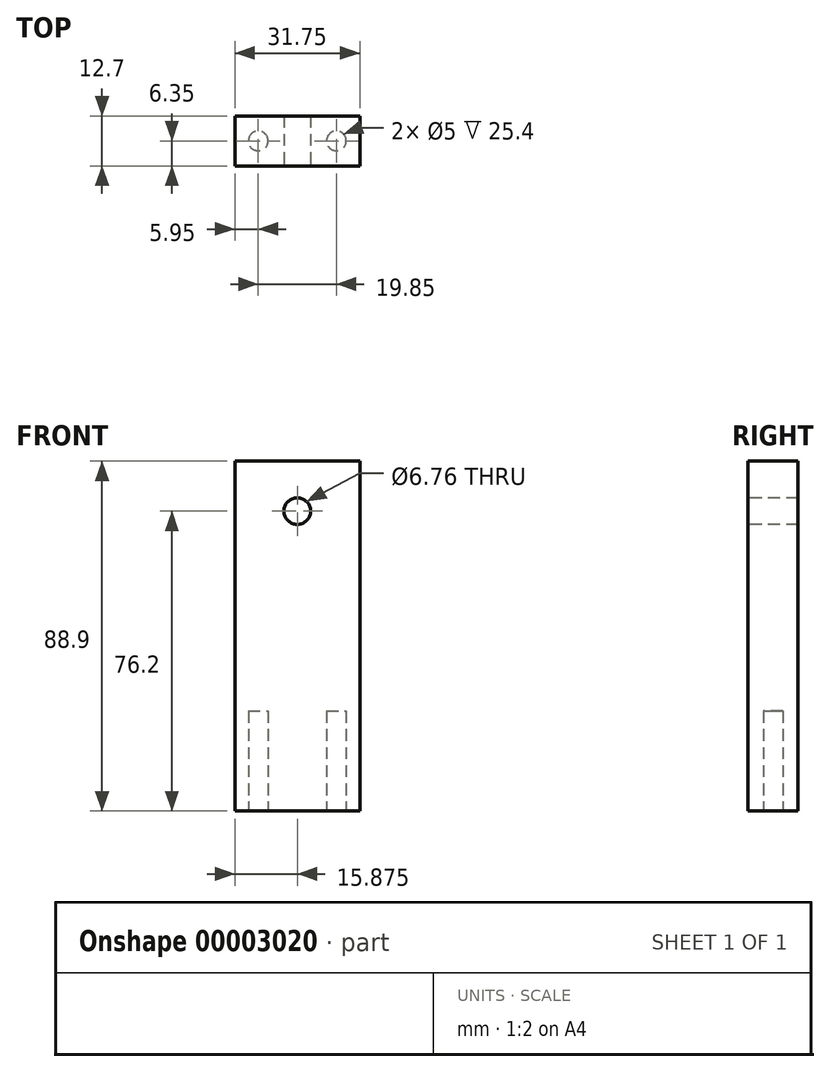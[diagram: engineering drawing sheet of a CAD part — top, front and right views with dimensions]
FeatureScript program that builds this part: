
annotation { "Feature Type Name" : "Feature", "Feature Type Description" : "" }
export const myFeature = defineFeature(function(context is Context, id is Id, definition is map)
    precondition{}
    {
        {
            var Q0;
            Q0=qCreatedBy(makeId("Top.planeOp"),FACE);
            var sketch = newSketch(context, id + "F0", { "sketchPlane" : qUnion([Q0])});
            skLineSegment(sketch, "E0.bottom", {"start": v(0, 0) * mm, "end": v(31.75, 0) * mm});
            skLineSegment(sketch, "E0.top", {"start": v(0, 12.7) * mm, "end": v(31.75, 12.7) * mm});
            skLineSegment(sketch, "E0.left", {"start": v(0, 0) * mm, "end": v(0, 12.7) * mm});
            skLineSegment(sketch, "E0.right", {"start": v(31.75, 0) * mm, "end": v(31.75, 12.7) * mm});
            skSolve(sketch);
        }
        {
            var Q0;
            Q0=makeQuery(id+"F0.imprint","IMPRINT",FACE,{"disambiguationData":[TD([[makeQuery(id+"F0.imprint","IMPRINT",EDGE,{"derivedFrom":sQuery(id+"F0.wireOp",EDGE,"E0.bottom")}),1.0]])]});
            extrude(context, id + "F1", {"entities" : qUnion([Q0]), "depth" : 88.9 * mm});
        }
        {
            var Q0;
            Q0=makeQuery(id+"F1.opExtrude","SWEPT_FACE",FACE,{"disambiguationData":[OSD([sQuery(id+"F0.wireOp",EDGE,"E0.bottom")])]});
            var sketch = newSketch(context, id + "F2", { "sketchPlane" : qUnion([Q0])});
            skCircle(sketch, "E1", {"center": v(15.88, 76.2) * mm, "radius": 3.38 * mm});
            skSolve(sketch);
        }
        {
            var Q0;
            Q0=makeQuery(id+"F2.imprint","IMPRINT",FACE,{"disambiguationData":[TD([[makeQuery(id+"F2.imprint","IMPRINT",EDGE,{"derivedFrom":sQuery(id+"F2.wireOp",EDGE,"E1")}),1.0]])]});
            extrude(context, id + "F3", {"entities" : qUnion([Q0]), "operationType" : NewBodyOperationType.REMOVE, "oppositeDirection" : true, "depth" : 25.4 * mm});
        }
        {
            var Q0;
            Q0=makeQuery(id+"F1.opExtrude","CAP_FACE",FACE,{"disambiguationData":[OSD([sQuery(id+"F0.wireOp",EDGE,"E0.bottom"),sQuery(id+"F0.wireOp",EDGE,"E0.top"),sQuery(id+"F0.wireOp",EDGE,"E0.left"),sQuery(id+"F0.wireOp",EDGE,"E0.right")])],"isStart":true});
            var sketch = newSketch(context, id + "F4", { "sketchPlane" : qUnion([Q0])});
            skCircle(sketch, "E2", {"center": v(5.95, -6.35) * mm, "radius": 2.5 * mm});
            skCircle(sketch, "E3", {"center": v(25.8, -6.35) * mm, "radius": 2.5 * mm});
            skSolve(sketch);
        }
        {
            var Q0;
            Q0=makeQuery(id+"F4.imprint","IMPRINT",FACE,{"disambiguationData":[TD([[makeQuery(id+"F4.imprint","IMPRINT",EDGE,{"derivedFrom":sQuery(id+"F4.wireOp",EDGE,"E2")}),1.0]])]});
            var Q1;
            Q1=makeQuery(id+"F4.imprint","IMPRINT",FACE,{"disambiguationData":[TD([[makeQuery(id+"F4.imprint","IMPRINT",EDGE,{"derivedFrom":sQuery(id+"F4.wireOp",EDGE,"E3")}),1.0]])]});
            extrude(context, id + "F5", {"entities" : qUnion([Q0, Q1]), "operationType" : NewBodyOperationType.REMOVE, "oppositeDirection" : true, "depth" : 25.4 * mm});
        }
    });
